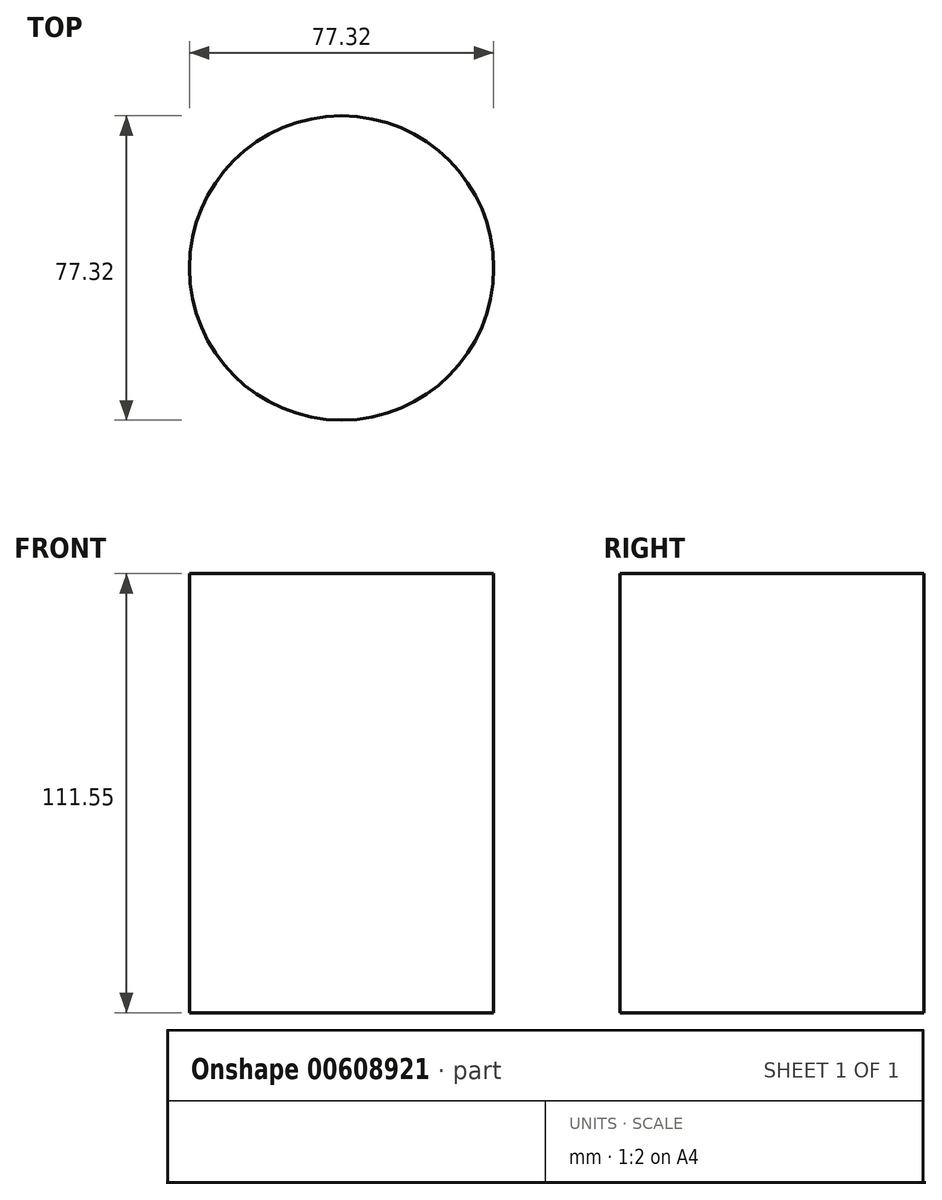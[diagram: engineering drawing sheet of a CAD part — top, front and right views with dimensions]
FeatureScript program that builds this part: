
annotation { "Feature Type Name" : "Feature", "Feature Type Description" : "" }
export const myFeature = defineFeature(function(context is Context, id is Id, definition is map)
    precondition{}
    {
        {
            var Q0;
            Q0=qCreatedBy(makeId("Top.planeOp"),FACE);
            var sketch = newSketch(context, id + "F0", { "sketchPlane" : qUnion([Q0])});
            skCircle(sketch, "E0", {"center": v(0.59, -0.04) * mm, "radius": 38.66 * mm});
            skPoint(sketch, "E0.first.point", {"position": v(0, 38.62) * mm});
            skPoint(sketch, "E0.second.point", {"position": v(0, -38.7) * mm});
            skPoint(sketch, "E0.third.point", {"position": v(39.25, 0) * mm});
            skSolve(sketch);
        }
        {
            var Q0;
            Q0 = qSketchRegion(id + "F0", true);
            extrude(context, id + "F1", {"entities" : qUnion([Q0]), "depth" : 60.75 * mm, "offsetDistance" : 25.4 * mm});
        }
        {
            var Q0;
            Q0=makeQuery(id+"F1.opExtrude","CAP_FACE",FACE,{"disambiguationData":[OSD([sQuery(id+"F0.wireOp",EDGE,"E0")])],"isStart":false});
            extrude(context, id + "F2", {"entities" : qUnion([Q0]), "operationType" : NewBodyOperationType.ADD, "depth" : 25.4 * mm, "offsetDistance" : 25.4 * mm});
        }
        {
            var Q0;
            Q0=makeQuery(id+"F2.opExtrude","CAP_FACE",FACE,{"disambiguationData":[OSD([sQuery(id+"F0.wireOp",EDGE,"E0")])],"isStart":false});
            extrude(context, id + "F3", {"entities" : qUnion([Q0]), "operationType" : NewBodyOperationType.ADD, "depth" : 25.4 * mm, "offsetDistance" : 25.4 * mm});
        }
    });
